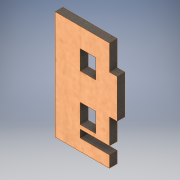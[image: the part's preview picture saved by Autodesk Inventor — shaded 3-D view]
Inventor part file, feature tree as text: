
AUTODESK INVENTOR PART (.ipt)
format: ipt  version: 2019 (Build 230136000, 136)  size: 146,432 bytes
history: native  units: mm
features: other x1, extrude x1, sketch x1
ambient origin geometry x8: Origin, YZ Plane, XZ Plane, XY Plane, X Axis, Y Axis, Z Axis, Center Point
bodies: Body1 (feature_tree)
feature tree (3):
  other  "Твердое тело1"
  extrude  "Выдавливание1"  Depth=4.0mm
  sketch  "Эскиз1"
